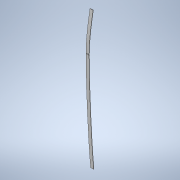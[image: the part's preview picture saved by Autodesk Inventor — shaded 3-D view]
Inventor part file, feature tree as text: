
AUTODESK INVENTOR PART (.ipt)
format: ipt  version: 2020.3 (Build 243373010, 373A)  size: 114,688 bytes
history: native  units: mm
features: other x2, extrude x1, sketch x1
ambient origin geometry x8: Origin, YZ Plane, XZ Plane, XY Plane, X Axis, Y Axis, Z Axis, Center Point
bodies: Solid1 (feature_tree)
feature tree (4):
  other  "cowl_strip.ipt"
  other  "base_sketch.ipt"
  extrude  "Extrusion1"  Depth=10.0mm
  sketch  "Sketch10"  dims[d0=10.0mm d1=10.0mm d2=9.0mm d3=0.0mm]
